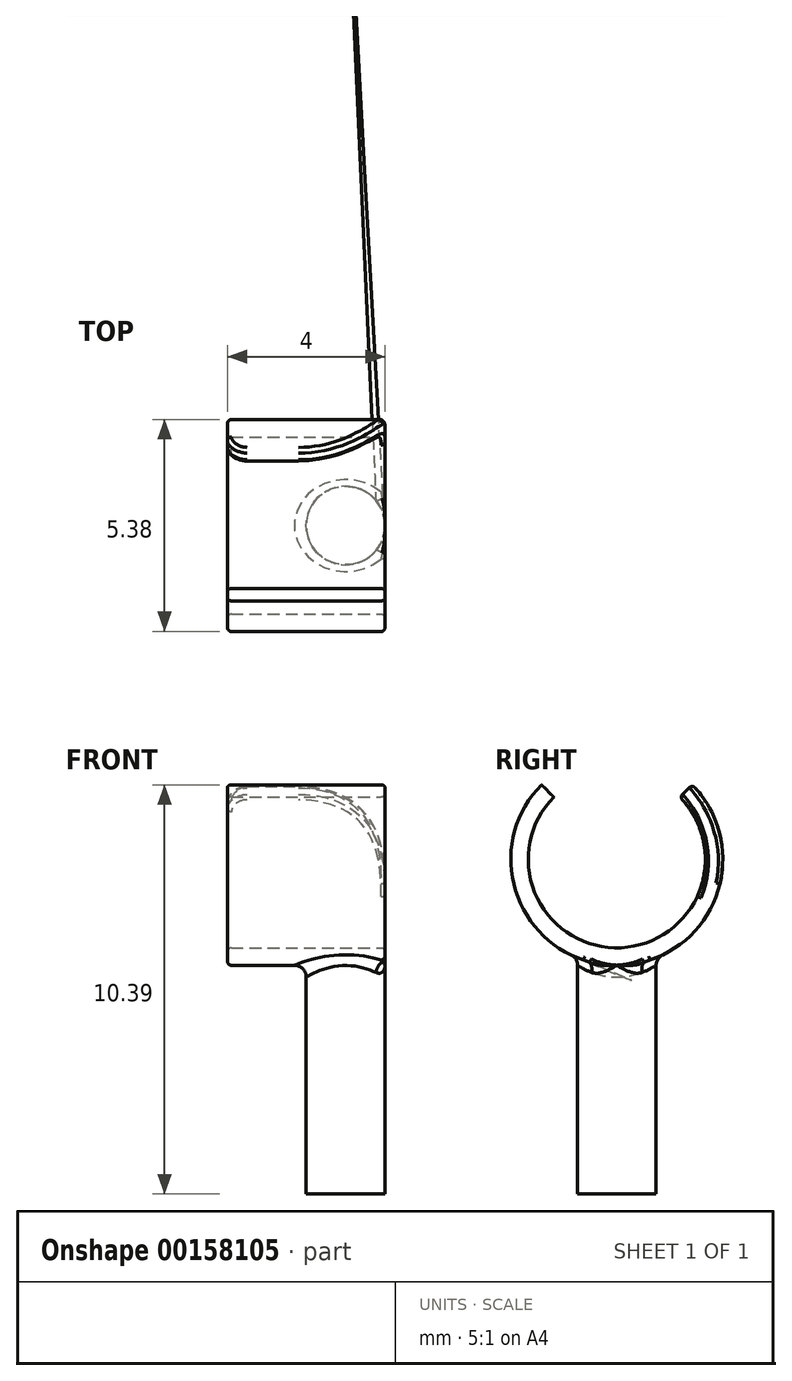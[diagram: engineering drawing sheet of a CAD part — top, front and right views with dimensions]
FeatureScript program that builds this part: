
annotation { "Feature Type Name" : "Feature", "Feature Type Description" : "" }
export const myFeature = defineFeature(function(context is Context, id is Id, definition is map)
    precondition{}
    {
        {
            var Q0;
            Q0=qCreatedBy(makeId("Top.planeOp"),FACE);
            var sketch = newSketch(context, id + "F0", { "sketchPlane" : qUnion([Q0])});
            skCircle(sketch, "E0", {"center": v(0, 0) * mm, "radius": 1 * mm});
            skSolve(sketch);
        }
        {
            var Q0;
            Q0=makeQuery(id+"F0.imprint","IMPRINT",FACE,{"disambiguationData":[TD([[makeQuery(id+"F0.imprint","IMPRINT",EDGE,{"derivedFrom":sQuery(id+"F0.wireOp",EDGE,"E0")}),1.0]])]});
            extrude(context, id + "F1", {"entities" : qUnion([Q0]), "depth" : 6 * mm});
        }
        {
            var Q0;
            Q0=qCreatedBy(makeId("Right.planeOp"),FACE);
            cPlane(context, id + "F2", {"entities" : qUnion([Q0]), "cplaneType" : CPlaneType.OFFSET, "offset" : 1 * mm, "width" : 150 * mm, "height" : 150 * mm});
        }
        {
            var Q0;
            Q0=qCreatedBy(id+"F2.planeOp",FACE);
            var sketch = newSketch(context, id + "F3", { "sketchPlane" : qUnion([Q0])});
            skArc(sketch, "E1", {"start": v(-1.6, 10.08) * mm, "mid": v(0, 6.25) * mm, "end": v(1.6, 10.08) * mm});
            skArc(sketch, "E2", {"start": v(-1.6, 10.67) * mm, "mid": v(0, 5.8) * mm, "end": v(1.6, 10.67) * mm});
            skLineSegment(sketch, "E3.0", {"start": v(-1, 6) * mm, "end": v(1, 6) * mm});
            skLineSegment(sketch, "E4", {"start": v(0, 8.5) * mm, "end": v(-3.52, 11.98) * mm});
            skLineSegment(sketch, "E5", {"start": v(-3.52, 11.98) * mm, "end": v(0, 8.5) * mm});
            skLineSegment(sketch, "E6", {"start": v(0, 8.5) * mm, "end": v(3.3, 11.76) * mm});
            skLineSegment(sketch, "E7", {"start": v(-1.6, 10.08) * mm, "end": v(-1.6, 10.67) * mm});
            skLineSegment(sketch, "E8", {"start": v(1.6, 10.08) * mm, "end": v(1.6, 10.67) * mm});
            skSolve(sketch);
        }
        {
            var Q0;
            {var subQ6=sQuery(id+"F3.wireOp",EDGE,"E1");Q0=makeQuery(id+"F3.imprint","IMPRINT",FACE,{"disambiguationData":[TD([[makeQuery(id+"F3.imprint","IMPRINT",EDGE,{"derivedFrom":subQ6}),-1.0]])]});}
            var Q1;
            {var subQ0=sQuery(id+"F3.wireOp",EDGE,"E3.0");Q1=makeQuery(id+"F3.imprint","IMPRINT",FACE,{"disambiguationData":[TD([[makeQuery(id+"F3.imprint","IMPRINT",EDGE,{"derivedFrom":subQ0}),-1.0]])]});}
            extrude(context, id + "F4", {"entities" : qUnion([Q0, Q1]), "operationType" : NewBodyOperationType.ADD, "oppositeDirection" : true, "depth" : 4 * mm});
        }
        {
            var Q0;
            Q0=makeQuery(id+"F4.boolean.opBoolean","INTERSECT",EDGE,{"derivedFrom":[makeQuery(id+"F1.opExtrude","SWEPT_FACE",FACE,{"disambiguationData":[OSD([sQuery(id+"F0.wireOp",EDGE,"E0")])]}),makeQuery(id+"F4.opExtrude","SWEPT_FACE",FACE,{"disambiguationData":[OSD([sQuery(id+"F3.wireOp",EDGE,"E2")])]})]});
            fillet(context, id + "F5", {"entities" : qUnion([Q0]), "radius" : 0.3 * mm, "tangentPropagation" : true, "allowEdgeOverflow" : false});
        }
        {
            var Q0;
            Q0=makeQuery(id+"F4.opExtrude","CAP_EDGE",EDGE,{"disambiguationData":[OSD([sQuery(id+"F3.wireOp",EDGE,"E6")])],"isStart":true});
            var Q1;
            Q1=makeQuery(id+"F4.opExtrude","CAP_EDGE",EDGE,{"disambiguationData":[OSD([sQuery(id+"F3.wireOp",EDGE,"E5")])],"isStart":true});
            fillet(context, id + "F6", {"entities" : qUnion([Q0, Q1]), "radius" : 2.2 * mm, "tangentPropagation" : true, "allowEdgeOverflow" : false});
        }
        {
            var Q0;
            Q0=makeQuery(id+"F4.opExtrude","CAP_EDGE",EDGE,{"disambiguationData":[OSD([sQuery(id+"F3.wireOp",EDGE,"E6")])],"isStart":false});
            var Q1;
            Q1=makeQuery(id+"F4.opExtrude","CAP_EDGE",EDGE,{"disambiguationData":[OSD([sQuery(id+"F3.wireOp",EDGE,"E5")])],"isStart":false});
            fillet(context, id + "F7", {"entities" : qUnion([Q0, Q1]), "radius" : 0.5 * mm, "tangentPropagation" : true, "allowEdgeOverflow" : false});
        }
        {
            var Q0;
            Q0=makeQuery(id+"F4.opExtrude","SWEPT_EDGE",EDGE,{"disambiguationData":[OSD([sQuery(id+"F3.wireOp",EDGE,"E1"),sQuery(id+"F3.wireOp",EDGE,"E6"),sQuery(id+"F3.wireOp",EDGE,"E8")])]});
            var Q1;
            Q1=makeQuery(id+"F4.opExtrude","SWEPT_EDGE",EDGE,{"disambiguationData":[OSD([sQuery(id+"F3.wireOp",EDGE,"E2"),sQuery(id+"F3.wireOp",EDGE,"E6")])]});
            fillet(context, id + "F8", {"entities" : qUnion([Q0, Q1]), "radius" : 0.1 * mm, "tangentPropagation" : true, "allowEdgeOverflow" : false});
        }
    });
